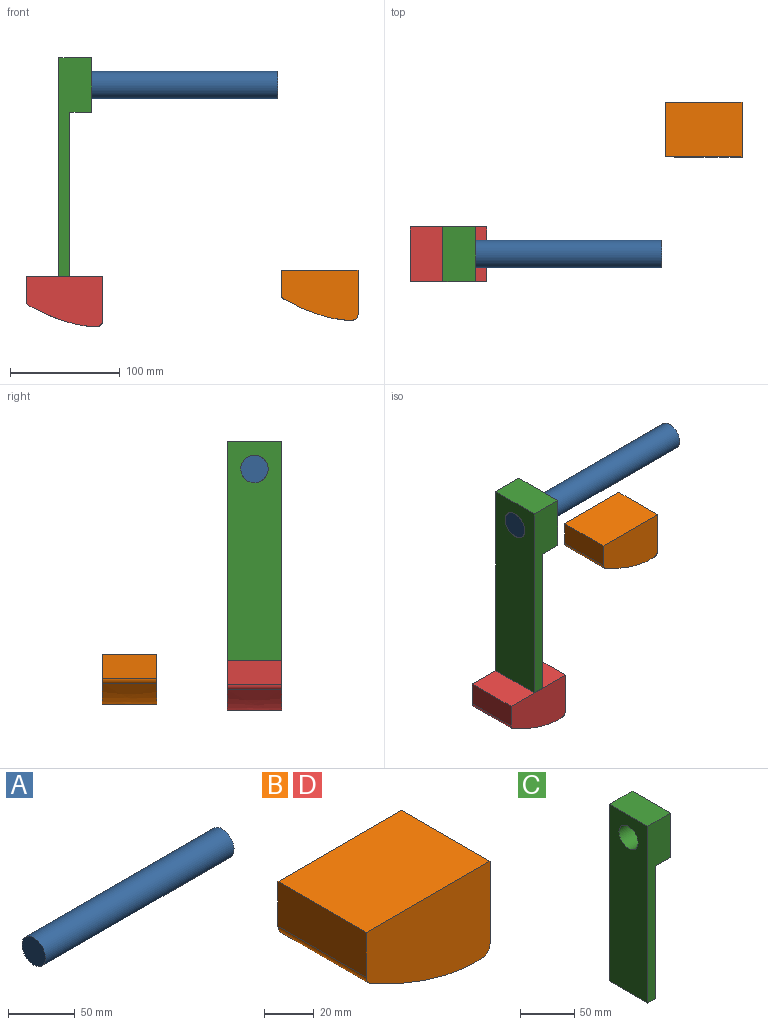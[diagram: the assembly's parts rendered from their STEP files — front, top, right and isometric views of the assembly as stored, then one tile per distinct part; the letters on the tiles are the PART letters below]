
ASSEMBLY  parts=4 mates=2
PART A: 3 faces, bbox 200x25x25 mm
  f0: cylinder r=12.5mm len=200mm, axis (-1,0,0), area 15708mm2, adj f1,f2
  f1: plane 25x25mm, normal (1,0,0), area 490.9mm2, adj f0
  f2: plane 25x25mm, normal (-1,0,0), area 490.9mm2, adj f0
PART B: 8 faces, bbox 70x50x46.5 mm
  f0: plane 50x22.01mm, normal (-1,0,0), area 1100.6mm2, adj f3,f4,f5,f6
  f1: extruded ~62.53x50mm, area 3303.6mm2, adj f4,f5,f6,f7
  f2: plane 50x40.36mm, normal (1,0,0), area 2018.2mm2, adj f3,f4,f5,f7
  f3: plane 70x50mm, normal (0,0,1), area 3500mm2, adj f0,f2,f4,f5
  f4: plane 70x46.45mm, normal (0,-1,0), area 2706.6mm2, adj f0,f1,f2,f3,f6,f7
  f5: plane 70x46.45mm, normal (0,1,0), area 2706.6mm2, adj f0,f1,f2,f3,f6,f7
  f6: cylinder r=5mm len=50mm, axis (0,1,0), area 270.4mm2, adj f0,f1,f4,f5
  f7: cylinder r=5mm len=50mm, axis (0,1,0), area 383.6mm2, adj f1,f2,f4,f5
PART C: 9 faces, bbox 30x50x200 mm
  f0: plane 50x10mm, normal (0,0,-1), area 500mm2, adj f1,f5,f6,f7
  f1: plane 150x50mm, normal (1,0,0), area 7500mm2, adj f0,f2,f6,f7
  f2: plane 50x20mm, normal (0,0,-1), area 1000mm2, adj f1,f3,f6,f7
  f3: plane 50x50mm, normal (1,0,0), area 2009.1mm2, adj f2,f4,f6,f7,f8
  f4: plane 50x30mm, normal (0,0,1), area 1500mm2, adj f3,f5,f6,f7
  f5: plane 200x50mm, normal (-1,0,0), area 9509.1mm2, adj f0,f4,f6,f7,f8
  f6: plane 200x30mm, normal (0,-1,0), area 3000mm2, adj f0,f1,f2,f3,f4,f5
  f7: plane 200x30mm, normal (0,1,0), area 3000mm2, adj f0,f1,f2,f3,f4,f5
  f8: cylinder r=12.5mm len=30mm, axis (1,0,0), area 2356.2mm2, adj f3,f5
PART D: same geometry as B
PLACE A t=(-89.32,-33.81,208.46)mm
PLACE B t=(113.7,105.09,14.18)mm
PLACE C t=(-89.32,-8.81,33.46)mm
PLACE D t=(-119.32,-8.81,8.46)mm
MATE revolute C.f8 <-> A.f0  axis (-1,0,0) through (-89.32,-33.81,208.46)mm
MATE planar C.f0 <-> D.f3  axis (0,0,-1) through (-84.32,-33.81,33.46)mm
